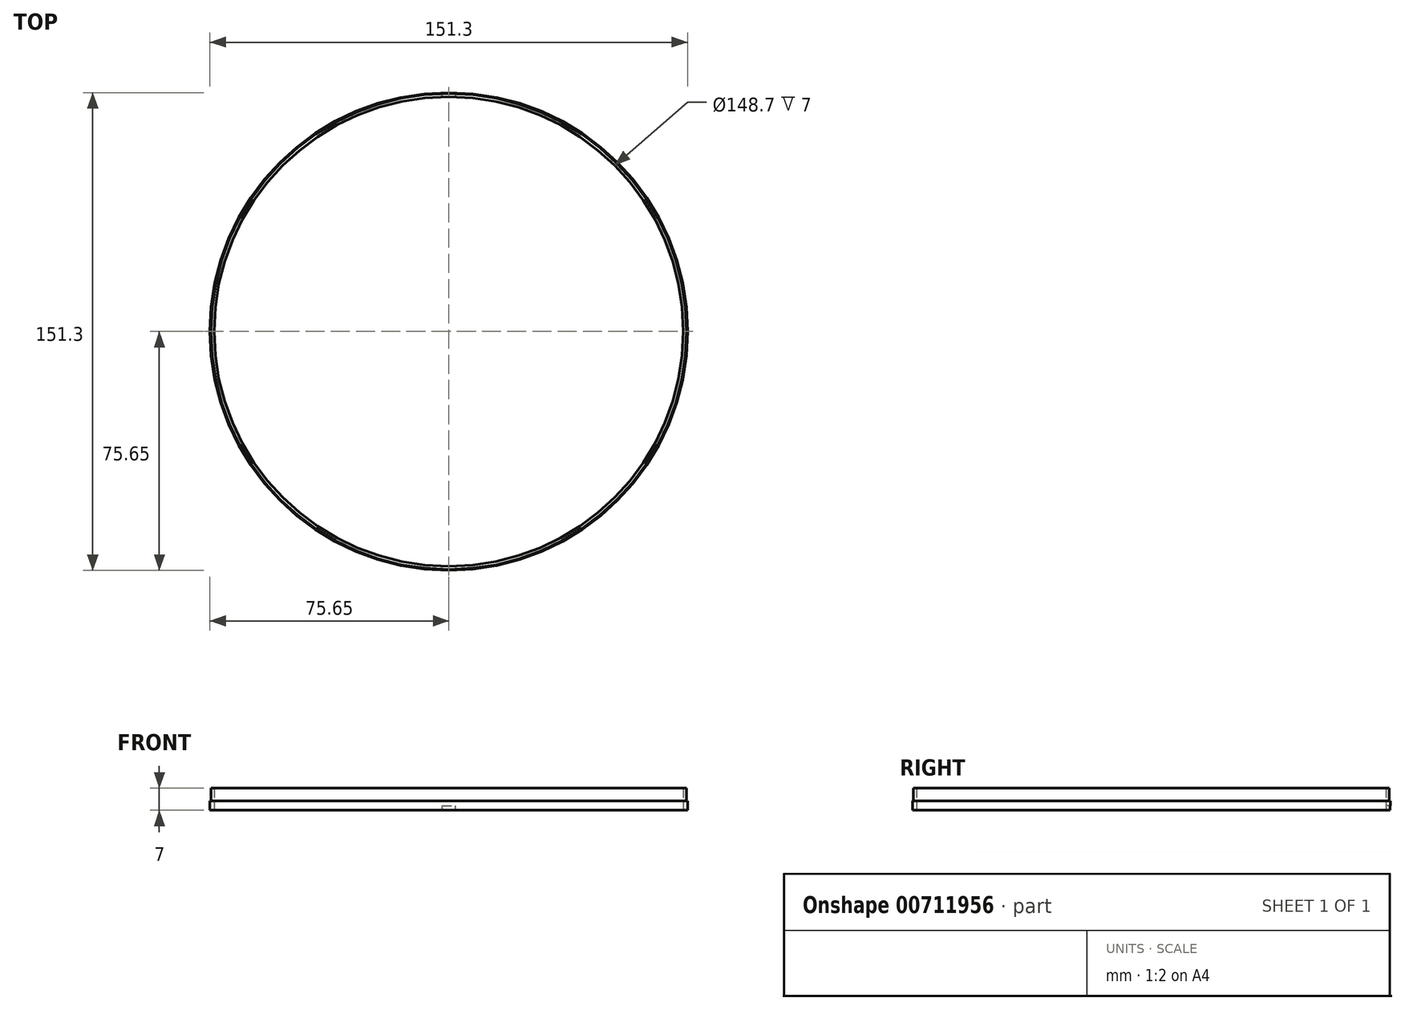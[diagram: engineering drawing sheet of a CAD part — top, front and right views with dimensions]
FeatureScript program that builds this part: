
annotation { "Feature Type Name" : "Feature", "Feature Type Description" : "" }
export const myFeature = defineFeature(function(context is Context, id is Id, definition is map)
    precondition{}
    {
        {
            var Q0;
            Q0=qCreatedBy(makeId("Right.planeOp"),FACE);
            var sketch = newSketch(context, id + "F0", { "sketchPlane" : qUnion([Q0])});
            skLineSegment(sketch, "E0", {"start": v(-74.35, 0) * mm, "end": v(-74.35, 7) * mm});
            skLineSegment(sketch, "E1", {"start": v(-74.35, 7) * mm, "end": v(-75.35, 7) * mm});
            skLineSegment(sketch, "E2", {"start": v(-75.35, 7) * mm, "end": v(-75.35, 3) * mm});
            skLineSegment(sketch, "E3", {"start": v(-75.65, 3) * mm, "end": v(-75.35, 3) * mm});
            skLineSegment(sketch, "E4", {"start": v(-75.65, 3) * mm, "end": v(-75.65, 0) * mm});
            skLineSegment(sketch, "E5", {"start": v(-75.65, 0) * mm, "end": v(-74.35, 0) * mm});
            skPoint(sketch, "E6", {"position": v(-75, 0) * mm});
            skLineSegment(sketch, "E7", {"start": v(0, 0) * mm, "end": v(0, 6.61) * mm, "construction": true});
            skSolve(sketch);
        }
        {
            var Q0;
            Q0 = qSketchRegion(id + "F0", true);
            var Q1;
            Q1=sQuery(id+"F0.wireOp",EDGE,"E7");
            revolve(context, id + "F1", {"surfaceOperationType" : NewSurfaceOperationType.NEW, "entities" : qUnion([Q0]), "axis" : qUnion([Q1]), "revolveType" : RevolveType.FULL});
        }
        {
            var Q0;
            Q0=qCreatedBy(makeId("Front.planeOp"),FACE);
            var sketch = newSketch(context, id + "F2", { "sketchPlane" : qUnion([Q0])});
            skLineSegment(sketch, "E8", {"start": v(0, 1.5) * mm, "end": v(2.1, 1.5) * mm});
            skLineSegment(sketch, "E9", {"start": v(2.1, 1.5) * mm, "end": v(2.1, 0) * mm});
            skLineSegment(sketch, "E10", {"start": v(2.1, 0) * mm, "end": v(0, 0) * mm});
            skLineSegment(sketch, "E11", {"start": v(0, 0) * mm, "end": v(0, 1.5) * mm});
            skLineSegment(sketch, "E12.MirrorCS", {"start": v(-2.1, 1.5) * mm, "end": v(-2.1, 0) * mm});
            skLineSegment(sketch, "E13.MirrorCS", {"start": v(-2.1, 0) * mm, "end": v(0, 0) * mm});
            skLineSegment(sketch, "E14.MirrorCS", {"start": v(0, 1.5) * mm, "end": v(-2.1, 1.5) * mm});
            skSolve(sketch);
        }
        {
            var Q0;
            Q0 = qSketchRegion(id + "F2", true);
            var Q1;
            Q1=makeQuery(id+"F1.opRevolve","SWEPT_FACE",FACE,{"disambiguationData":[OSD([sQuery(id+"F0.wireOp",EDGE,"E2")])]});
            var Q2;
            Q2=makeQuery(id+"FaJeTHPjDP9lbKw_0.opShell","OFFSET_FACE",FACE,{"disambiguationData":[OSD([sQuery(id+"Fzp027vN8NkeUAl_0.wireOp",EDGE,"J0gwppCI-Z5Zv-imRS-cOnP-yT7ZRkTKJPiU")])]});
            extrude(context, id + "F3", {"entities" : qUnion([Q0]), "operationType" : NewBodyOperationType.REMOVE, "endBound" : BoundingType.THROUGH_ALL, "oppositeDirection" : true, "depth" : 25 * mm, "endBoundEntityFace" : qUnion([Q1]), "offsetDistance" : 80 * mm, "offsetOppositeDirection" : true});
        }
    });
